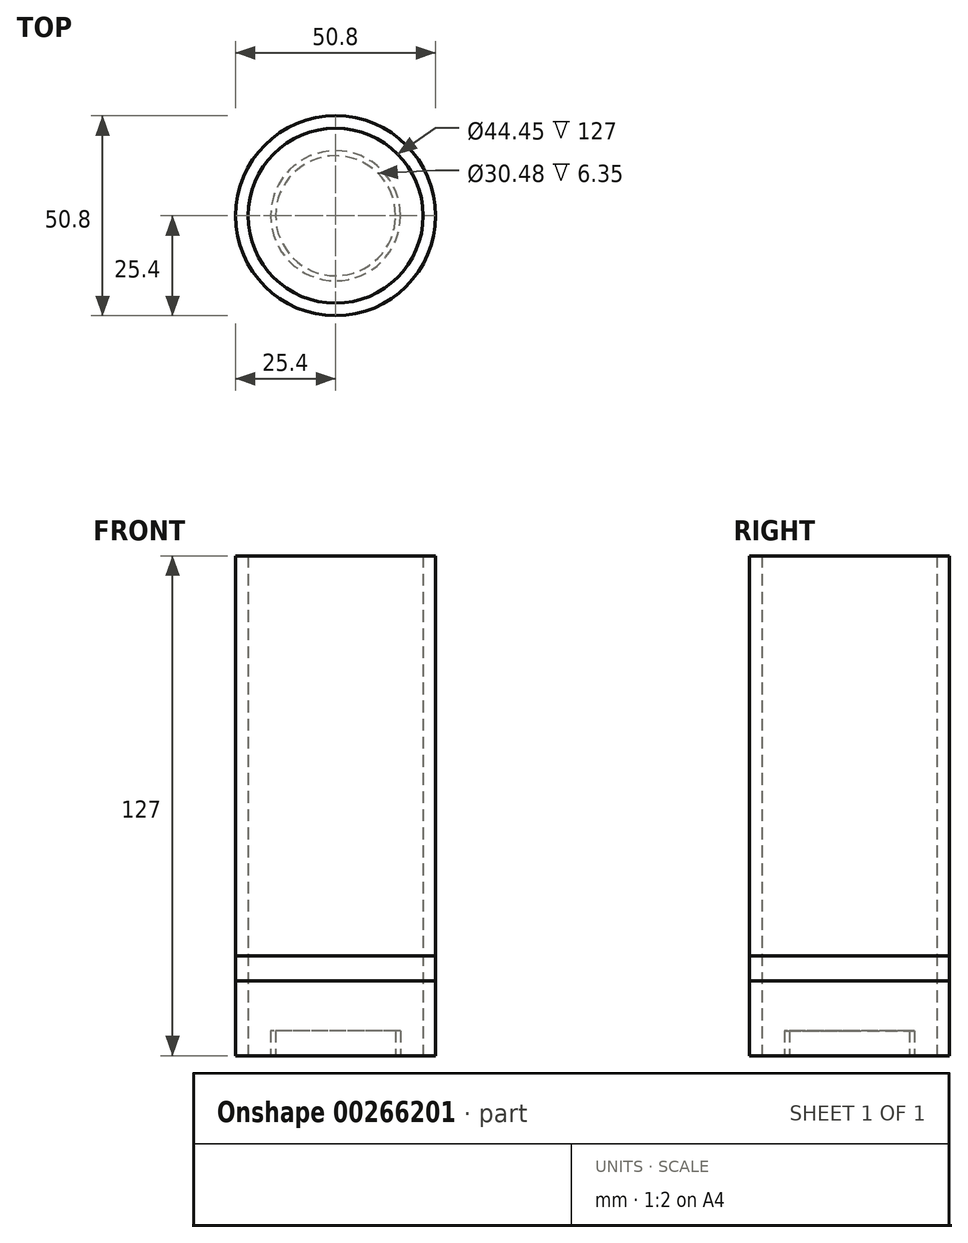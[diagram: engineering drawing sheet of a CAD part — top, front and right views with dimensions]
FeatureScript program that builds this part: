
annotation { "Feature Type Name" : "Feature", "Feature Type Description" : "" }
export const myFeature = defineFeature(function(context is Context, id is Id, definition is map)
    precondition{}
    {
        {
            var Q0;
            Q0=qCreatedBy(makeId("Top.planeOp"),FACE);
            var sketch = newSketch(context, id + "F0", { "sketchPlane" : qUnion([Q0])});
            skCircle(sketch, "E0", {"center": v(0, 0) * mm, "radius": 25.4 * mm});
            skSolve(sketch);
        }
        {
            var Q0;
            Q0=makeQuery(id+"F0.imprint","IMPRINT",FACE,{"disambiguationData":[TD([[makeQuery(id+"F0.imprint","IMPRINT",EDGE,{"derivedFrom":sQuery(id+"F0.wireOp",EDGE,"E0")}),1.0]])]});
            extrude(context, id + "F1", {"entities" : qUnion([Q0]), "depth" : 19.05 * mm});
        }
        {
            var Q0;
            Q0=qCreatedBy(makeId("Top.planeOp"),FACE);
            var sketch = newSketch(context, id + "F2", { "sketchPlane" : qUnion([Q0])});
            skCircle(sketch, "E1", {"center": v(0, 0) * mm, "radius": 25.4 * mm});
            skCircle(sketch, "E2", {"center": v(0, 0) * mm, "radius": 22.23 * mm});
            skSolve(sketch);
        }
        {
            var Q0;
            Q0=makeQuery(id+"F2.imprint","IMPRINT",FACE,{"disambiguationData":[TD([[makeQuery(id+"F2.imprint","IMPRINT",EDGE,{"derivedFrom":sQuery(id+"F2.wireOp",EDGE,"E1")}),1.0]])]});
            extrude(context, id + "F3", {"entities" : qUnion([Q0]), "depth" : 127 * mm});
        }
        {
            var Q0;
            Q0=qCreatedBy(makeId("Top.planeOp"),FACE);
            var sketch = newSketch(context, id + "F4", { "sketchPlane" : qUnion([Q0])});
            skCircle(sketch, "E3", {"center": v(0, 0) * mm, "radius": 16.51 * mm});
            skCircle(sketch, "E4", {"center": v(0, 0) * mm, "radius": 15.24 * mm});
            skSolve(sketch);
        }
        {
            var Q0;
            Q0 = qSketchRegion(id + "F4", true);
            var Q1;
            Q1=makeQuery(id+"F1.opExtrude","CAP_FACE",FACE,{"disambiguationData":[OSD([sQuery(id+"F0.wireOp",EDGE,"E0")])],"isStart":false});
            extrude(context, id + "F5", {"entities" : qUnion([Q0, Q1]), "depth" : 6.35 * mm});
        }
    });
